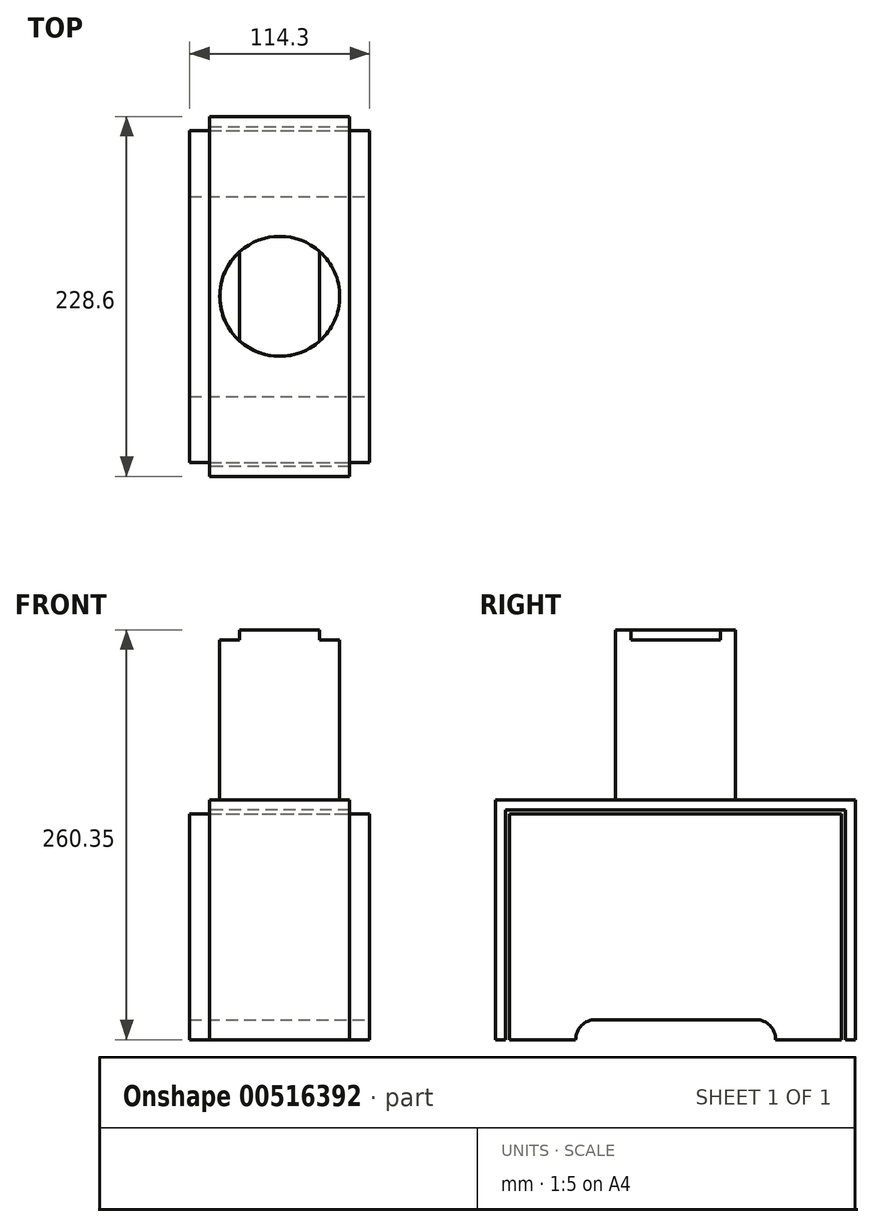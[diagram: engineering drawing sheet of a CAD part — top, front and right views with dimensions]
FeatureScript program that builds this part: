
annotation { "Feature Type Name" : "Feature", "Feature Type Description" : "" }
export const myFeature = defineFeature(function(context is Context, id is Id, definition is map)
    precondition{}
    {
        {
            var Q0;
            Q0=qCreatedBy(makeId("Top.planeOp"),FACE);
            var sketch = newSketch(context, id + "F0", { "sketchPlane" : qUnion([Q0])});
            skLineSegment(sketch, "E0.bottom", {"start": v(-57.15, 105.41) * mm, "end": v(57.15, 105.41) * mm});
            skLineSegment(sketch, "E0.top", {"start": v(-57.15, -105.4) * mm, "end": v(57.15, -105.4) * mm});
            skLineSegment(sketch, "E0.left", {"start": v(-57.15, 105.41) * mm, "end": v(-57.15, -105.4) * mm});
            skLineSegment(sketch, "E0.right", {"start": v(57.15, 105.41) * mm, "end": v(57.15, -105.4) * mm});
            skSolve(sketch);
        }
        {
            var Q0;
            Q0 = qSketchRegion(id + "F0", true);
            extrude(context, id + "F1", {"entities" : qUnion([Q0]), "depth" : 143.5 * mm, "offsetDistance" : 25.4 * mm});
        }
        {
            var Q0;
            Q0=makeQuery(id+"F1.opExtrude","CAP_FACE",FACE,{"disambiguationData":[OSD([sQuery(id+"F0.wireOp",EDGE,"E0.bottom"),sQuery(id+"F0.wireOp",EDGE,"E0.top"),sQuery(id+"F0.wireOp",EDGE,"E0.left"),sQuery(id+"F0.wireOp",EDGE,"E0.right")])],"isStart":false});
            var sketch = newSketch(context, id + "F2", { "sketchPlane" : qUnion([Q0])});
            skLineSegment(sketch, "E1.bottom", {"start": v(-44.45, 114.3) * mm, "end": v(44.45, 114.3) * mm});
            skLineSegment(sketch, "E1.top", {"start": v(-44.45, -114.3) * mm, "end": v(44.45, -114.3) * mm});
            skLineSegment(sketch, "E1.left", {"start": v(-44.45, 114.3) * mm, "end": v(-44.45, -114.3) * mm});
            skLineSegment(sketch, "E1.right", {"start": v(44.45, 114.3) * mm, "end": v(44.45, -114.3) * mm});
            skSolve(sketch);
        }
        {
            var Q0;
            {var subQ0=sQuery(id+"F2.wireOp",EDGE,"E1.left");var subQ1=makeQuery(id+"F1.opExtrude","CAP_EDGE",EDGE,{"disambiguationData":[OSD([sQuery(id+"F0.wireOp",EDGE,"E0.bottom")])],"isStart":false});var subQ2=makeQuery(id+"F2.imprint","INTERSECT",VERTEX,{"derivedFrom":[subQ1,subQ0]});Q0=makeQuery(id+"F2.imprint","IMPRINT",FACE,{"disambiguationData":[TD([[makeQuery(id+"F2.imprint","IMPRINT",EDGE,{"disambiguationData":[TD([[subQ2,-1.0]])],"derivedFrom":subQ0}),1.0]])]});}
            var Q1;
            {var subQ0=sQuery(id+"F2.wireOp",EDGE,"E1.bottom");Q1=makeQuery(id+"F2.imprint","IMPRINT",FACE,{"disambiguationData":[TD([[makeQuery(id+"F2.imprint","IMPRINT",EDGE,{"derivedFrom":subQ0}),-1.0]])]});}
            var Q2;
            {var subQ0=sQuery(id+"F2.wireOp",EDGE,"E1.top");Q2=makeQuery(id+"F2.imprint","IMPRINT",FACE,{"disambiguationData":[TD([[makeQuery(id+"F2.imprint","IMPRINT",EDGE,{"derivedFrom":subQ0}),1.0]])]});}
            extrude(context, id + "F3", {"entities" : qUnion([Q0, Q1, Q2]), "operationType" : NewBodyOperationType.ADD, "depth" : 8.9 * mm, "offsetDistance" : 25.4 * mm});
        }
        {
            var Q0;
            {var subQ0=sQuery(id+"F0.wireOp",EDGE,"E0.bottom");Q0=makeQuery(id+"F3.boolean.opBoolean","MERGE",FACE,{"derivedFrom":[makeQuery(id+"F1.opExtrude","SWEPT_FACE",FACE,{"disambiguationData":[OSD([subQ0])]}),makeQuery(id+"F3.opExtrude","SWEPT_FACE",FACE,{"disambiguationData":[OSD([subQ0])]})]});}
            var sketch = newSketch(context, id + "F4", { "sketchPlane" : qUnion([Q0])});
            skLineSegment(sketch, "E2.bottom", {"start": v(-44.45, 152.4) * mm, "end": v(44.45, 152.4) * mm});
            skLineSegment(sketch, "E2.top", {"start": v(-44.45, 146.05) * mm, "end": v(44.45, 146.05) * mm});
            skLineSegment(sketch, "E2.left", {"start": v(-44.45, 152.4) * mm, "end": v(-44.45, 146.05) * mm});
            skLineSegment(sketch, "E2.right", {"start": v(44.45, 152.4) * mm, "end": v(44.45, 146.05) * mm});
            skLineSegment(sketch, "E3.top", {"start": v(-44.45, 143.51) * mm, "end": v(44.45, 143.51) * mm});
            skLineSegment(sketch, "E3.left", {"start": v(-44.45, 146.05) * mm, "end": v(-44.45, 143.51) * mm});
            skLineSegment(sketch, "E3.right", {"start": v(44.45, 146.05) * mm, "end": v(44.45, 143.51) * mm});
            skSolve(sketch);
        }
        {
            var Q0;
            Q0=makeQuery(id+"F4.imprint","IMPRINT",FACE,{"disambiguationData":[TD([[makeQuery(id+"F4.imprint","IMPRINT",EDGE,{"derivedFrom":sQuery(id+"F4.wireOp",EDGE,"E2.top")}),-1.0]])]});
            extrude(context, id + "F5", {"entities" : qUnion([Q0]), "operationType" : NewBodyOperationType.REMOVE, "oppositeDirection" : true, "depth" : 228.6 * mm, "offsetDistance" : 25.4 * mm});
        }
        {
            var Q0;
            Q0=makeQuery(id+"F3.opExtrude","CAP_FACE",FACE,{"disambiguationData":[OSD([sQuery(id+"F2.wireOp",EDGE,"E1.bottom"),sQuery(id+"F2.wireOp",EDGE,"E1.top"),sQuery(id+"F2.wireOp",EDGE,"E1.left"),sQuery(id+"F2.wireOp",EDGE,"E1.right")])],"isStart":false});
            var sketch = newSketch(context, id + "F6", { "sketchPlane" : qUnion([Q0])});
            skLineSegment(sketch, "E4.bottom", {"start": v(-44.45, 114.3) * mm, "end": v(44.45, 114.3) * mm});
            skLineSegment(sketch, "E4.top", {"start": v(-44.45, 107.95) * mm, "end": v(44.45, 107.95) * mm});
            skLineSegment(sketch, "E4.left", {"start": v(-44.45, 114.3) * mm, "end": v(-44.45, 107.95) * mm});
            skLineSegment(sketch, "E4.right", {"start": v(44.45, 114.3) * mm, "end": v(44.45, 107.95) * mm});
            skLineSegment(sketch, "E5.bottom", {"start": v(-44.45, -114.3) * mm, "end": v(44.45, -114.3) * mm});
            skLineSegment(sketch, "E5.top", {"start": v(-44.45, -107.95) * mm, "end": v(44.45, -107.95) * mm});
            skLineSegment(sketch, "E5.left", {"start": v(-44.45, -114.3) * mm, "end": v(-44.45, -107.95) * mm});
            skLineSegment(sketch, "E5.right", {"start": v(44.45, -114.3) * mm, "end": v(44.45, -107.95) * mm});
            skSolve(sketch);
        }
        {
            var Q0;
            Q0 = qSketchRegion(id + "F6", true);
            extrude(context, id + "F7", {"entities" : qUnion([Q0]), "operationType" : NewBodyOperationType.ADD, "oppositeDirection" : true, "depth" : 152.4 * mm, "offsetDistance" : 25.4 * mm});
        }
        {
            var Q0;
            Q0=makeQuery(id+"F7.boolean.opBoolean","MERGE",FACE,{"derivedFrom":[makeQuery(id+"F3.opExtrude","SWEPT_FACE",FACE,{"disambiguationData":[OSD([sQuery(id+"F2.wireOp",EDGE,"E1.right")])]}),makeQuery(id+"F7.opExtrude","SWEPT_FACE",FACE,{"disambiguationData":[OSD([sQuery(id+"F6.wireOp",EDGE,"E4.right")])]}),makeQuery(id+"F7.opExtrude","SWEPT_FACE",FACE,{"disambiguationData":[OSD([sQuery(id+"F6.wireOp",EDGE,"E5.right")])]})]});
            var sketch = newSketch(context, id + "F8", { "sketchPlane" : qUnion([Q0])});
            skLineSegment(sketch, "E6.bottom", {"start": v(107.95, 146.05) * mm, "end": v(105.41, 146.05) * mm});
            skLineSegment(sketch, "E6.top", {"start": v(107.95, 143.51) * mm, "end": v(105.41, 143.51) * mm});
            skLineSegment(sketch, "E6.left", {"start": v(107.95, 146.05) * mm, "end": v(107.95, 143.51) * mm});
            skLineSegment(sketch, "E6.right", {"start": v(105.41, 146.05) * mm, "end": v(105.41, 143.51) * mm});
            skSolve(sketch);
        }
        {
            var Q0;
            Q0 = qSketchRegion(id + "F8", true);
            extrude(context, id + "F9", {"entities" : qUnion([Q0]), "operationType" : NewBodyOperationType.REMOVE, "oppositeDirection" : true, "depth" : 88.9 * mm, "offsetDistance" : 25.4 * mm});
        }
        {
            var Q0;
            Q0=makeQuery(id+"F3.opExtrude","CAP_FACE",FACE,{"disambiguationData":[OSD([sQuery(id+"F2.wireOp",EDGE,"E1.bottom"),sQuery(id+"F2.wireOp",EDGE,"E1.top"),sQuery(id+"F2.wireOp",EDGE,"E1.left"),sQuery(id+"F2.wireOp",EDGE,"E1.right")])],"isStart":false});
            var sketch = newSketch(context, id + "F10", { "sketchPlane" : qUnion([Q0])});
            skCircle(sketch, "E7", {"center": v(0, 0) * mm, "radius": 38.1 * mm});
            skSolve(sketch);
        }
        {
            var Q0;
            Q0 = qSketchRegion(id + "F10", true);
            extrude(context, id + "F11", {"entities" : qUnion([Q0]), "operationType" : NewBodyOperationType.ADD, "depth" : 101.6 * mm, "offsetDistance" : 25.4 * mm});
        }
        {
            var Q0;
            Q0=makeQuery(id+"F11.opExtrude","CAP_FACE",FACE,{"disambiguationData":[OSD([sQuery(id+"F10.wireOp",EDGE,"E7")])],"isStart":false});
            var sketch = newSketch(context, id + "F12", { "sketchPlane" : qUnion([Q0])});
            skLineSegment(sketch, "E8.left", {"start": v(-25.4, 28.4) * mm, "end": v(-25.4, -28.4) * mm});
            skLineSegment(sketch, "E8.right", {"start": v(25.4, 28.4) * mm, "end": v(25.4, -28.4) * mm});
            skArc(sketch, "E9", {"start": v(25.4, 28.4) * mm, "mid": v(0, 38.1) * mm, "end": v(-25.4, 28.4) * mm});
            skPoint(sketch, "E9.first.point", {"position": v(-25.4, 28.4) * mm});
            skPoint(sketch, "E9.second.point", {"position": v(25.4, 28.4) * mm});
            skPoint(sketch, "E9.third.point", {"position": v(-11.22, -36.4) * mm});
            skPoint(sketch, "E10.orphan", {"position": v(-25.4, -47.56) * mm});
            skArc(sketch, "E11.trimOffspring", {"start": v(-25.4, -28.4) * mm, "mid": v(0, -38.1) * mm, "end": v(25.4, -28.4) * mm});
            skSolve(sketch);
        }
        {
            var Q0;
            Q0 = qSketchRegion(id + "F12", true);
            extrude(context, id + "F13", {"entities" : qUnion([Q0]), "operationType" : NewBodyOperationType.ADD, "depth" : 6.35 * mm, "offsetDistance" : 25.4 * mm});
        }
        {
            var Q0;
            Q0=makeQuery(id+"F1.opExtrude","SWEPT_FACE",FACE,{"disambiguationData":[OSD([sQuery(id+"F0.wireOp",EDGE,"E0.right")])]});
            var sketch = newSketch(context, id + "F14", { "sketchPlane" : qUnion([Q0])});
            skLineSegment(sketch, "E12.bottom", {"start": v(-63.5, 0) * mm, "end": v(63.5, 0) * mm});
            skLineSegment(sketch, "E12.top", {"start": v(-50.8, 12.7) * mm, "end": v(50.8, 12.7) * mm});
            skPoint(sketch, "E13", {"position": v(-50.8, 12.7) * mm});
            skPoint(sketch, "E14", {"position": v(50.8, 12.7) * mm});
            skArc(sketch, "E15", {"start": v(-50.8, 12.7) * mm, "mid": v(-59.78, 8.98) * mm, "end": v(-63.5, 0) * mm});
            skArc(sketch, "E16", {"start": v(63.5, 0) * mm, "mid": v(59.78, 8.98) * mm, "end": v(50.8, 12.7) * mm});
            skPoint(sketch, "E12.left.end.orphan", {"position": v(-63.5, 12.7) * mm});
            skPoint(sketch, "E17.orphan", {"position": v(63.5, 12.7) * mm});
            skSolve(sketch);
        }
        {
            var Q0;
            Q0 = qSketchRegion(id + "F14", true);
            extrude(context, id + "F15", {"entities" : qUnion([Q0]), "operationType" : NewBodyOperationType.REMOVE, "oppositeDirection" : true, "depth" : 114.3 * mm, "offsetDistance" : 25.4 * mm});
        }
    });
